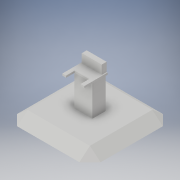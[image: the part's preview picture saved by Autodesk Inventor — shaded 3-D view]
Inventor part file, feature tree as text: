
AUTODESK INVENTOR PART (.ipt)
format: ipt  version: 2017 (Build 210142000, 142)  size: 402,944 bytes
history: native  units: in
note: dims shown in document units (in); Inventor stores cm internally (conversion verified against a paired STEP export)
features: other x10, extrude x8, sketch x7, pattern_circular x2, loft x2, plane x1
ambient origin geometry x7: Origin, YZ Plane, XY Plane, X Axis, Y Axis, Z Axis, Center Point
bodies: Solid4 (feature_tree)
feature tree (30):
  other  "bace + terminal"
  extrude  "Extrusion16"  Depth=1.0in
  extrude  "arm rests and terminal monitor"  Depth=0.85in
  other  "middle of the part vertical"
  other  "used to line up the key board and mouse"
  extrude  "bace"  Depth=0.75in
  extrude  "ramp to terminal"  Depth=1.0in
  pattern_circular  "made rest of ramps to terminal"  [2 undecoded]
  loft  "smooth edges of base"
  pattern_circular  "rest of the smooth edges of base"  [2 undecoded]
  other  "mate to back to monitor"
  extrude  "monitor raise"  Depth=0.2083in TaperAngle=0.0deg
  sketch  "Sketch26"  dims[d27=1.1in d28=0.75in]
  plane  "Work Plane20"
  loft  "outlet cap"
  sketch  "Sketch28"  dims[d29=1.0in d30=0.65in]
  extrude  "outlet revele out"  Depth=0.0181in
  extrude  "hot and ground wire holes"  Depth=1.125in
  other  "screw workplane"
  other  "screw made"
  extrude  "slot for screw"  Depth=1.0in TaperAngle=0.0deg
  other  "bottom workplane"
  other  "bace of terminal"
  sketch  "Sketch23"  dims[d0=1.0in d1=0.75in]
  sketch  "Sketch25"  dims[d19=1.2in d20=0.85in]
  sketch  "Sketch29"  dims[d42=1.1in d43=0.85in d44=1.0in d45=0.75in d49=1.2in d50=0.85in d51=1.0in d52=0.75in]
  sketch  "Sketch30"  dims[d123=1.0in d124=0.0in]
  sketch  "Sketch31"  dims[d163=0.8125in d165=0.4167in d166=0.8125in d167=0.4167in d168=0.2083in d169=0.0in d170=1.125in d173=1.8892in d175=1.125in d178=1.0in d179=0.0in d182=0.2318in d183=0.3777in d185=0.05in d186=0.0678in d188=0.1962in d189=0.3421in d190=0.0in d191=90.0deg d192=0.0in d193=90.0deg d194=0.0251in d195=0.0305in d197=0.0931in d198=0.0311in d199=0.0362in d200=0.0045in d201=0.0208in d202=0.0208in d203=0.0078in d204=0.0291in d205=0.0078in d206=0.0362in d207=0.0045in d208=0.0208in d209=0.0078in d211=0.0078in d212=0.0208in d213=0.0181in d214=0.0291in d221=0.003in d222=0.0in d223=0.0649in d224=0.0in d225=90.0deg d226=0.0108in d227=0.0027in d228=90.0deg d229=0.0015in d230=0.0128in d231=0.0in d232=3.6493in d233=0.0in d234=0.1564in d235=0.2069in d236=7.0in d237=7.0in d238=0.2749in d239=3.6493in d240=0.0in d241=1.5748in d242=360.0deg d244=0.0in d245=0.5527in d246=2.2315in d247=0.1134in d248=0.0181in d253=0.0in d254=90.0deg d255=0.0in d256=90.0deg d257=1.5748in d258=360.0deg]
  other  "Edges4"
  other  "Edges5"
note: 4 required parameter values undecoded (feature->parameter linkage not recoverable at this tier; creation-order binding heuristic only, values carry confidence <= 0.55)
